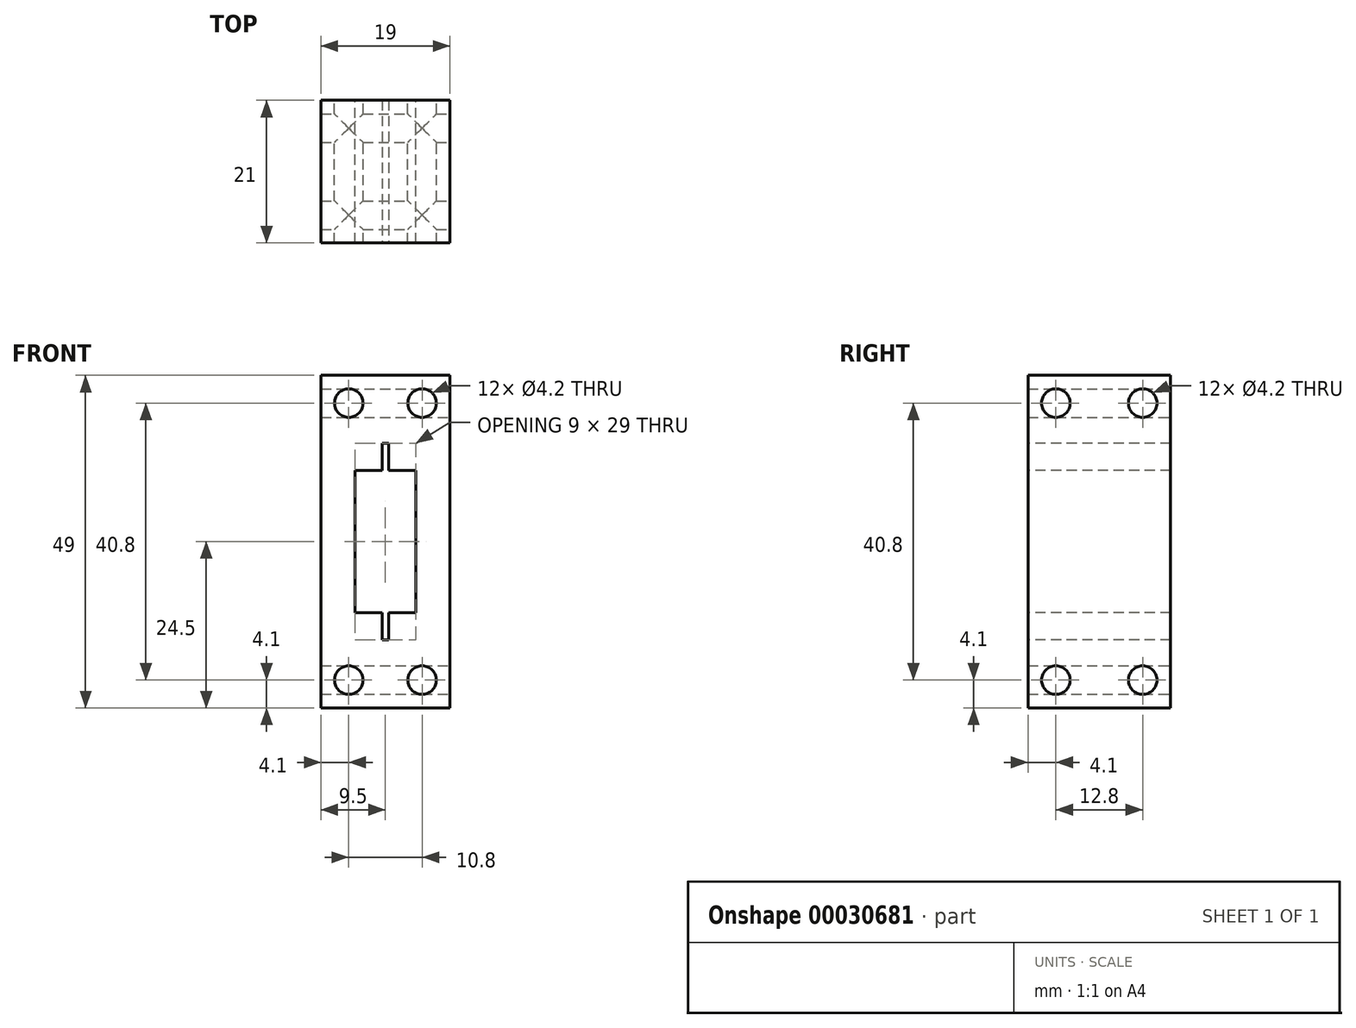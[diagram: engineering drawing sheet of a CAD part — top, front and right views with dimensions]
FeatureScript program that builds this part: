
annotation { "Feature Type Name" : "Feature", "Feature Type Description" : "" }
export const myFeature = defineFeature(function(context is Context, id is Id, definition is map)
    precondition{}
    {
        {
            var Q0;
            Q0=qCreatedBy(makeId("Front.planeOp"),FACE);
            var sketch = newSketch(context, id + "F0", { "sketchPlane" : qUnion([Q0])});
            skLineSegment(sketch, "E0.bottom", {"start": v(-31.5, 35) * mm, "end": v(-12.5, 35) * mm});
            skLineSegment(sketch, "E0.top", {"start": v(-31.5, -14) * mm, "end": v(-12.5, -14) * mm});
            skLineSegment(sketch, "E0.left", {"start": v(-31.5, 35) * mm, "end": v(-31.5, -14) * mm});
            skLineSegment(sketch, "E0.right", {"start": v(-12.5, 35) * mm, "end": v(-12.5, -14) * mm});
            skLineSegment(sketch, "E1", {"start": v(-31.5, 10.5) * mm, "end": v(-12.5, 10.5) * mm, "construction": true});
            skLineSegment(sketch, "E2", {"start": v(-22, -14) * mm, "end": v(-22, 35) * mm, "construction": true});
            skLineSegment(sketch, "E3.rect.bottom", {"start": v(-17.5, 0) * mm, "end": v(-26.5, 0) * mm});
            skLineSegment(sketch, "E3.rect.top", {"start": v(-17.5, 21) * mm, "end": v(-26.5, 21) * mm});
            skLineSegment(sketch, "E3.rect.left", {"start": v(-17.5, 0) * mm, "end": v(-17.5, 21) * mm});
            skLineSegment(sketch, "E3.rect.right", {"start": v(-26.5, 0) * mm, "end": v(-26.5, 21) * mm});
            skPoint(sketch, "E3.rect.middle", {"position": v(-22, 10.5) * mm});
            skSolve(sketch);
        }
        {
            var Q0;
            Q0=makeQuery(id+"F0.imprint","IMPRINT",FACE,{"disambiguationData":[TD([[makeQuery(id+"F0.imprint","IMPRINT",EDGE,{"derivedFrom":sQuery(id+"F0.wireOp",EDGE,"E0.bottom")}),-1.0]])]});
            extrude(context, id + "F1", {"entities" : qUnion([Q0]), "depth" : 21 * mm});
        }
        {
            var Q0;
            Q0=makeQuery(id+"F1.opExtrude","CAP_FACE",FACE,{"disambiguationData":[OSD([sQuery(id+"F0.wireOp",EDGE,"E0.bottom"),sQuery(id+"F0.wireOp",EDGE,"E0.top"),sQuery(id+"F0.wireOp",EDGE,"E0.left"),sQuery(id+"F0.wireOp",EDGE,"E0.right"),sQuery(id+"F0.wireOp",EDGE,"E3.rect.bottom"),sQuery(id+"F0.wireOp",EDGE,"E3.rect.top"),sQuery(id+"F0.wireOp",EDGE,"E3.rect.left"),sQuery(id+"F0.wireOp",EDGE,"E3.rect.right")])],"isStart":false});
            var sketch = newSketch(context, id + "F2", { "sketchPlane" : qUnion([Q0])});
            skLineSegment(sketch, "E4", {"start": v(-22, 21) * mm, "end": v(-22, 35) * mm, "construction": true});
            skLineSegment(sketch, "E5.bottom", {"start": v(-22.5, 21) * mm, "end": v(-21.5, 21) * mm});
            skLineSegment(sketch, "E5.top", {"start": v(-22.5, 25) * mm, "end": v(-21.5, 25) * mm});
            skLineSegment(sketch, "E5.left", {"start": v(-22.5, 21) * mm, "end": v(-22.5, 25) * mm});
            skLineSegment(sketch, "E5.right", {"start": v(-21.5, 21) * mm, "end": v(-21.5, 25) * mm});
            skLineSegment(sketch, "E6.MirrorCS", {"start": v(-21.5, 0) * mm, "end": v(-21.5, -4) * mm});
            skLineSegment(sketch, "E7.MirrorCS", {"start": v(-22.5, 0) * mm, "end": v(-22.5, -4) * mm});
            skLineSegment(sketch, "E8.MirrorCS", {"start": v(-22.5, 0) * mm, "end": v(-21.5, 0) * mm});
            skLineSegment(sketch, "E9.MirrorCS", {"start": v(-22.5, -4) * mm, "end": v(-21.5, -4) * mm});
            skSolve(sketch);
        }
        {
            var Q0;
            Q0 = qSketchRegion(id + "F2", true);
            extrude(context, id + "F3", {"entities" : qUnion([Q0]), "operationType" : NewBodyOperationType.REMOVE, "oppositeDirection" : true, "depth" : 25 * mm});
        }
        {
            var Q0;
            Q0=makeQuery(id+"F1.opExtrude","CAP_FACE",FACE,{"disambiguationData":[OSD([sQuery(id+"F0.wireOp",EDGE,"E0.bottom"),sQuery(id+"F0.wireOp",EDGE,"E0.top"),sQuery(id+"F0.wireOp",EDGE,"E0.left"),sQuery(id+"F0.wireOp",EDGE,"E0.right"),sQuery(id+"F0.wireOp",EDGE,"E3.rect.bottom"),sQuery(id+"F0.wireOp",EDGE,"E3.rect.top"),sQuery(id+"F0.wireOp",EDGE,"E3.rect.left"),sQuery(id+"F0.wireOp",EDGE,"E3.rect.right")])],"isStart":true});
            var sketch = newSketch(context, id + "F4", { "sketchPlane" : qUnion([Q0])});
            skCircle(sketch, "E10", {"center": v(16.6, 30.9) * mm, "radius": 2.1 * mm});
            skLineSegment(sketch, "E11", {"start": v(22, 35) * mm, "end": v(22, -14) * mm, "construction": true});
            skLineSegment(sketch, "E12", {"start": v(12.5, 10.5) * mm, "end": v(31.5, 10.5) * mm, "construction": true});
            skCircle(sketch, "E13.MirrorC", {"center": v(16.6, -9.9) * mm, "radius": 2.1 * mm});
            skCircle(sketch, "E14.MirrorC", {"center": v(27.4, -9.9) * mm, "radius": 2.1 * mm});
            skCircle(sketch, "E15.MirrorC", {"center": v(27.4, 30.9) * mm, "radius": 2.1 * mm});
            skSolve(sketch);
        }
        {
            var Q0;
            Q0 = qSketchRegion(id + "F4", true);
            extrude(context, id + "F5", {"entities" : qUnion([Q0]), "operationType" : NewBodyOperationType.REMOVE, "oppositeDirection" : true, "depth" : 25 * mm});
        }
        {
            var Q0;
            Q0=makeQuery(id+"F1.opExtrude","SWEPT_FACE",FACE,{"disambiguationData":[OSD([sQuery(id+"F0.wireOp",EDGE,"E0.right")])]});
            var sketch = newSketch(context, id + "F6", { "sketchPlane" : qUnion([Q0])});
            skCircle(sketch, "E16", {"center": v(-16.9, 30.9) * mm, "radius": 2.1 * mm});
            skLineSegment(sketch, "E17", {"start": v(-10.5, 35) * mm, "end": v(-10.5, -14) * mm, "construction": true});
            skLineSegment(sketch, "E18", {"start": v(-21, 10.5) * mm, "end": v(0, 10.5) * mm, "construction": true});
            skCircle(sketch, "E19.MirrorC", {"center": v(-16.9, -9.9) * mm, "radius": 2.1 * mm});
            skCircle(sketch, "E20.MirrorC", {"center": v(-4.1, 30.9) * mm, "radius": 2.1 * mm});
            skCircle(sketch, "E21.MirrorC", {"center": v(-4.1, -9.9) * mm, "radius": 2.1 * mm});
            skSolve(sketch);
        }
        {
            var Q0;
            Q0 = qSketchRegion(id + "F6", true);
            extrude(context, id + "F7", {"entities" : qUnion([Q0]), "operationType" : NewBodyOperationType.REMOVE, "oppositeDirection" : true, "depth" : 25 * mm});
        }
    });
